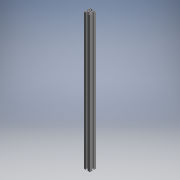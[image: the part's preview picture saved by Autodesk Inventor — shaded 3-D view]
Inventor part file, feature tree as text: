
AUTODESK INVENTOR PART (.ipt)
format: ipt  version: 2017.3 (Build 213256000, 256)  size: 209,920 bytes
history: native  units: mm (DEFAULTED — no unit token found)
features: other x21, sketch x3, hole x2, extrude x1, pattern_linear x1
ambient origin geometry x8: Origin, YZ Plane, XZ Plane, XY Plane, X Axis, Y Axis, Z Axis, Center Point
bodies: Solid1 (feature_tree)
feature tree (28):
  extrude  "Extrusion1"  Depth=650.0mm
  hole  "Hole1"  [1 undecoded]
  hole  "Hole2"  [1 undecoded]
  pattern_linear  "Rectangular Pattern1"  [2 undecoded]
  other  "C1_XY"
  other  "C1_YZ"
  other  "C1_ZX"
  other  "C1_X"
  other  "C1_Y"
  other  "C1_Z"
  other  "C1_Center"
  other  "to_frame_cap1_XY"
  other  "to_frame_cap1_YZ"
  other  "to_frame_cap1_ZX"
  other  "to_frame_cap1_X"
  other  "to_frame_cap1_Y"
  other  "to_frame_cap1_Z"
  other  "to_frame_cap1_Center"
  other  "to_frame_cap2_XY"
  other  "to_frame_cap2_YZ"
  other  "to_frame_cap2_ZX"
  other  "to_frame_cap2_X"
  other  "to_frame_cap2_Y"
  other  "to_frame_cap2_Z"
  other  "to_frame_cap2_Center"
  sketch  "Sketch_1"  dims[d0=650.0mm d1=0.0mm]
  sketch  "Sketch2"  dims[d2=6.8mm d3=6.0mm d4=4.0mm d5=2.0mm d6=90.0deg d7=650.0mm d8=0.0mm]
  sketch  "Sketch3"  dims[d9=4.2mm d10=6.0mm d11=4.0mm d12=2.0mm d13=90.0deg d14=650.0mm d15=0.0mm d16=20.0mm d18=23.2mm d19=20.0mm d21=23.2mm d22=0.0mm d23=0.0mm d24=0.0mm]
note: 4 required parameter values undecoded (feature->parameter linkage not recoverable at this tier; creation-order binding heuristic only, values carry confidence <= 0.55)
